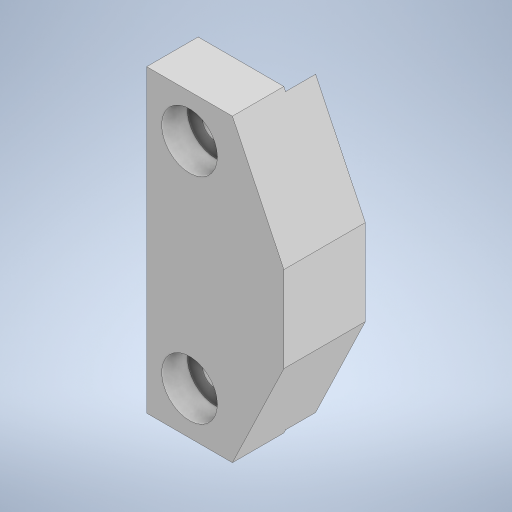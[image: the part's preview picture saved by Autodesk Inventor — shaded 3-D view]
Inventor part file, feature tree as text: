
AUTODESK INVENTOR PART (.ipt)
format: ipt  version: 2024 (Build 280153000, 153)  size: 293,376 bytes
history: native  units: mm
features: extrude x4, sketch x4, projected_geometry x4
ambient origin geometry x8: Origin, YZ Plane, XZ Plane, XY Plane, X Axis, Y Axis, Z Axis, Center Point
bodies: Solid1 (feature_tree)
feature tree (12):
  extrude  "Extrusion1"  Depth=25.0mm
  extrude  "Extrusion2"  Depth=10.0mm
  extrude  "Extrusion3"  Depth=3.0mm
  extrude  "Extrusion4"  Depth=6.0mm
  sketch  "Sketch1"  dims[d0=5.0mm d1=25.0mm]
  sketch  "Sketch2"  dims[d2=5.0mm d3=10.0mm]
  projected_geometry  "Projected Loop1"
  sketch  "Sketch3"  dims[d4=5.0mm d5=3.0mm]
  projected_geometry  "Projected Loop2"
  sketch  "Sketch4"  dims[d6=3.0mm d7=6.0mm d8=5.0mm d9=5.0mm d10=6.0mm d11=0.0mm d12=3.5mm d13=0.0mm d14=6.5mm d15=3.0mm d16=0.0mm d17=6.5mm d36=6.0mm d39=3.0mm d41=90.0deg d42=3.0mm d43=90.0deg d45=2.9mm d46=2.0mm d47=2.0mm d48=8.0mm d49=0.0mm d52=8.217909mm d54=0.2mm d55=2.9mm d56=0.2mm d57=6.0mm d53=0.5mm]
  projected_geometry  "Projected Loop3"
  projected_geometry  "Projected Loop4"
